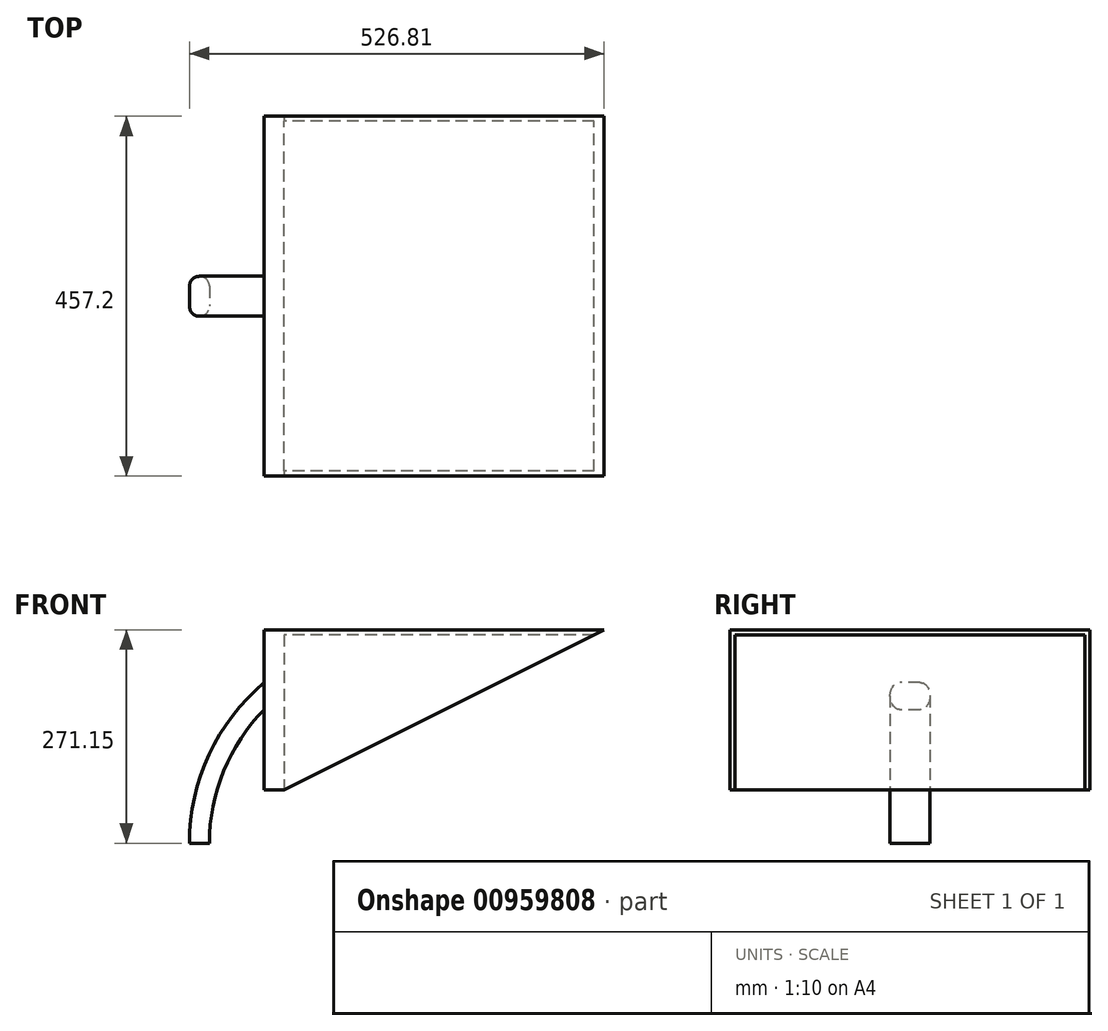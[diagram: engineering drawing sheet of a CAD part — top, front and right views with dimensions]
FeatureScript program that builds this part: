
annotation { "Feature Type Name" : "Feature", "Feature Type Description" : "" }
export const myFeature = defineFeature(function(context is Context, id is Id, definition is map)
    precondition{}
    {
        {
            var Q0;
            Q0=qCreatedBy(makeId("Top.planeOp"),FACE);
            var sketch = newSketch(context, id + "F0", { "sketchPlane" : qUnion([Q0])});
            skLineSegment(sketch, "E0.bottom", {"start": v(12.7, 12.7) * mm, "end": v(-12.7, 12.7) * mm});
            skLineSegment(sketch, "E0.top", {"start": v(12.7, -12.7) * mm, "end": v(-12.7, -12.7) * mm});
            skLineSegment(sketch, "E0.left", {"start": v(12.7, 12.7) * mm, "end": v(12.7, -12.7) * mm});
            skLineSegment(sketch, "E0.right", {"start": v(-12.7, 12.7) * mm, "end": v(-12.7, -12.7) * mm});
            skPoint(sketch, "E0.middle", {"position": v(0, 0) * mm});
            skCircle(sketch, "E1", {"center": v(0, 12.7) * mm, "radius": 12.7 * mm});
            skCircle(sketch, "E2", {"center": v(0, -12.7) * mm, "radius": 12.7 * mm});
            skLineSegment(sketch, "E3", {"start": v(254, -45.46) * mm, "end": v(254, 37.7) * mm, "construction": true});
            skSolve(sketch);
        }
        {
            var Q0;
            {var subQ0=sQuery(id+"F0.wireOp",EDGE,"E0.bottom");Q0=makeQuery(id+"F0.imprint","IMPRINT",FACE,{"disambiguationData":[TD([[makeQuery(id+"F0.imprint","IMPRINT",EDGE,{"derivedFrom":subQ0}),-1.0]])]});}
            var Q1;
            {var subQ0=sQuery(id+"F0.wireOp",EDGE,"E0.bottom");Q1=makeQuery(id+"F0.imprint","IMPRINT",FACE,{"disambiguationData":[TD([[makeQuery(id+"F0.imprint","IMPRINT",EDGE,{"derivedFrom":subQ0}),1.0]])]});}
            var Q2;
            {var subQ0=sQuery(id+"F0.wireOp",EDGE,"E0.right");Q2=makeQuery(id+"F0.imprint","IMPRINT",FACE,{"disambiguationData":[TD([[makeQuery(id+"F0.imprint","IMPRINT",EDGE,{"derivedFrom":subQ0}),1.0]])]});}
            var Q3;
            {var subQ0=sQuery(id+"F0.wireOp",EDGE,"E0.top");Q3=makeQuery(id+"F0.imprint","IMPRINT",FACE,{"disambiguationData":[TD([[makeQuery(id+"F0.imprint","IMPRINT",EDGE,{"derivedFrom":subQ0}),-1.0]])]});}
            var Q4;
            {var subQ0=sQuery(id+"F0.wireOp",EDGE,"E0.top");Q4=makeQuery(id+"F0.imprint","IMPRINT",FACE,{"disambiguationData":[TD([[makeQuery(id+"F0.imprint","IMPRINT",EDGE,{"derivedFrom":subQ0}),1.0]])]});}
            var Q5;
            {var subQ0=sQuery(id+"F0.wireOp",EDGE,"E0.left");Q5=makeQuery(id+"F0.imprint","IMPRINT",FACE,{"disambiguationData":[TD([[makeQuery(id+"F0.imprint","IMPRINT",EDGE,{"derivedFrom":subQ0}),-1.0]])]});}
            var Q6;
            Q6=sQuery(id+"F0.wireOp",EDGE,"E3");
            revolve(context, id + "F1", {"surfaceOperationType" : NewSurfaceOperationType.NEW, "entities" : qUnion([Q0, Q1, Q2, Q3, Q4, Q5]), "axis" : qUnion([Q6]), "revolveType" : RevolveType.ONE_DIRECTION, "angle" : 50 * degree});
        }
        {
            var Q0;
            Q0=qCreatedBy(makeId("Front.planeOp"),FACE);
            var sketch = newSketch(context, id + "F2", { "sketchPlane" : qUnion([Q0])});
            skLineSegment(sketch, "E4", {"start": v(82.31, 209.73) * mm, "end": v(82.31, 161.48) * mm});
            skLineSegment(sketch, "E5", {"start": v(82.31, 209.73) * mm, "end": v(106.04, 182.26) * mm});
            skLineSegment(sketch, "E6", {"start": v(106.04, 182.26) * mm, "end": v(82.31, 161.48) * mm});
            skSolve(sketch);
        }
        {
            var Q0;
            Q0=makeQuery(id+"F2.imprint","IMPRINT",FACE,{"disambiguationData":[TD([[makeQuery(id+"F2.imprint","IMPRINT",EDGE,{"derivedFrom":sQuery(id+"F2.wireOp",EDGE,"E4")}),1.0]])]});
            extrude(context, id + "F3", {"entities" : qUnion([Q0]), "operationType" : NewBodyOperationType.REMOVE, "oppositeDirection" : true, "depth" : 25.4 * mm, "offsetDistance" : 25.4 * mm, "hasSecondDirection" : true, "secondDirectionOppositeDirection" : false, "secondDirectionDepth" : 25.4 * mm});
        }
        {
            var Q0;
            Q0=makeQuery(id+"F3.boolean.opBoolean","COPY",FACE,{"derivedFrom":makeQuery(id+"F3.opExtrude","SWEPT_FACE",FACE,{"disambiguationData":[OSD([sQuery(id+"F2.wireOp",EDGE,"E4")])]})});
            var sketch = newSketch(context, id + "F4", { "sketchPlane" : qUnion([Q0])});
            skLineSegment(sketch, "E7.bottom", {"start": v(-228.6, 271.15) * mm, "end": v(228.6, 271.15) * mm});
            skLineSegment(sketch, "E7.top", {"start": v(-228.6, 67.95) * mm, "end": v(228.6, 67.95) * mm});
            skLineSegment(sketch, "E7.left", {"start": v(-228.6, 271.15) * mm, "end": v(-228.6, 67.95) * mm});
            skLineSegment(sketch, "E7.right", {"start": v(228.6, 271.15) * mm, "end": v(228.6, 67.95) * mm});
            skPoint(sketch, "E7.middle", {"position": v(0, 169.55) * mm});
            skSolve(sketch);
        }
        {
            var Q0;
            Q0=makeQuery(id+"F4.imprint","IMPRINT",FACE,{"disambiguationData":[TD([[makeQuery(id+"F4.imprint","IMPRINT",EDGE,{"derivedFrom":sQuery(id+"F4.wireOp",EDGE,"E7.bottom")}),-1.0]])]});
            var Q1;
            {var subQ0=makeQuery(id+"F3.opExtrude","SWEPT_FACE",FACE,{"disambiguationData":[OSD([sQuery(id+"F2.wireOp",EDGE,"E4")])]});Q1=makeQuery(id+"F4.imprint","IMPRINT",FACE,{"disambiguationData":[TD([[makeQuery(id+"F4.imprint","IMPRINT",EDGE,{"derivedFrom":makeQuery(id+"F3.boolean.opBoolean","INTERSECT",EDGE,{"derivedFrom":[makeQuery(id+"F1.opRevolve","SWEPT_FACE",FACE,{"disambiguationData":[OSD([sQuery(id+"F0.wireOp",EDGE,"E0.left")])]}),subQ0]})}),1.0]])]});}
            extrude(context, id + "F5", {"entities" : qUnion([Q0, Q1]), "operationType" : NewBodyOperationType.ADD, "depth" : 25.4 * mm, "offsetDistance" : 25.4 * mm});
        }
        {
            var Q0;
            Q0=makeQuery(id+"F5.opExtrude","CAP_FACE",FACE,{"disambiguationData":[OSD([sQuery(id+"F4.wireOp",EDGE,"E7.bottom"),sQuery(id+"F4.wireOp",EDGE,"E7.top"),sQuery(id+"F4.wireOp",EDGE,"E7.left"),sQuery(id+"F4.wireOp",EDGE,"E7.right")])],"isStart":false});
            var sketch = newSketch(context, id + "F6", { "sketchPlane" : qUnion([Q0])});
            skLineSegment(sketch, "E8.bottom", {"start": v(-222.25, 264.8) * mm, "end": v(222.25, 264.8) * mm});
            skLineSegment(sketch, "E8.top", {"start": v(-222.25, 67.95) * mm, "end": v(222.25, 67.95) * mm});
            skLineSegment(sketch, "E8.left", {"start": v(-222.25, 264.8) * mm, "end": v(-222.25, 67.95) * mm});
            skLineSegment(sketch, "E8.right", {"start": v(222.25, 264.8) * mm, "end": v(222.25, 67.95) * mm});
            skPoint(sketch, "E8.middle", {"position": v(0, 166.38) * mm});
            skSolve(sketch);
        }
        {
            var Q0;
            Q0=makeQuery(id+"F6.imprint","IMPRINT",FACE,{"disambiguationData":[TD([[makeQuery(id+"F6.imprint","IMPRINT",EDGE,{"derivedFrom":sQuery(id+"F6.wireOp",EDGE,"E8.bottom")}),1.0]])]});
            extrude(context, id + "F7", {"entities" : qUnion([Q0]), "operationType" : NewBodyOperationType.ADD, "depth" : 406.4 * mm, "offsetDistance" : 25.4 * mm});
        }
        {
            var Q0;
            {var subQ0=sQuery(id+"F4.wireOp",EDGE,"E7.left");Q0=makeQuery(id+"F7.boolean.opBoolean","MERGE",FACE,{"derivedFrom":[makeQuery(id+"F5.opExtrude","SWEPT_FACE",FACE,{"disambiguationData":[OSD([subQ0])]}),makeQuery(id+"F7.opExtrude","SWEPT_FACE",FACE,{"disambiguationData":[OSD([subQ0])]})]});}
            var sketch = newSketch(context, id + "F8", { "sketchPlane" : qUnion([Q0])});
            skLineSegment(sketch, "E9", {"start": v(82.31, 67.95) * mm, "end": v(107.71, 67.95) * mm});
            skLineSegment(sketch, "E10", {"start": v(107.71, 67.95) * mm, "end": v(514.11, 271.15) * mm});
            skSolve(sketch);
        }
        {
            var Q0;
            {var subQ0=sQuery(id+"F8.wireOp",EDGE,"E10");Q0=makeQuery(id+"F8.imprint","IMPRINT",FACE,{"disambiguationData":[TD([[makeQuery(id+"F8.imprint","IMPRINT",EDGE,{"derivedFrom":subQ0}),-1.0]])]});}
            extrude(context, id + "F9", {"entities" : qUnion([Q0]), "operationType" : NewBodyOperationType.REMOVE, "oppositeDirection" : true, "depth" : 457.2 * mm, "offsetDistance" : 25.4 * mm});
        }
    });
